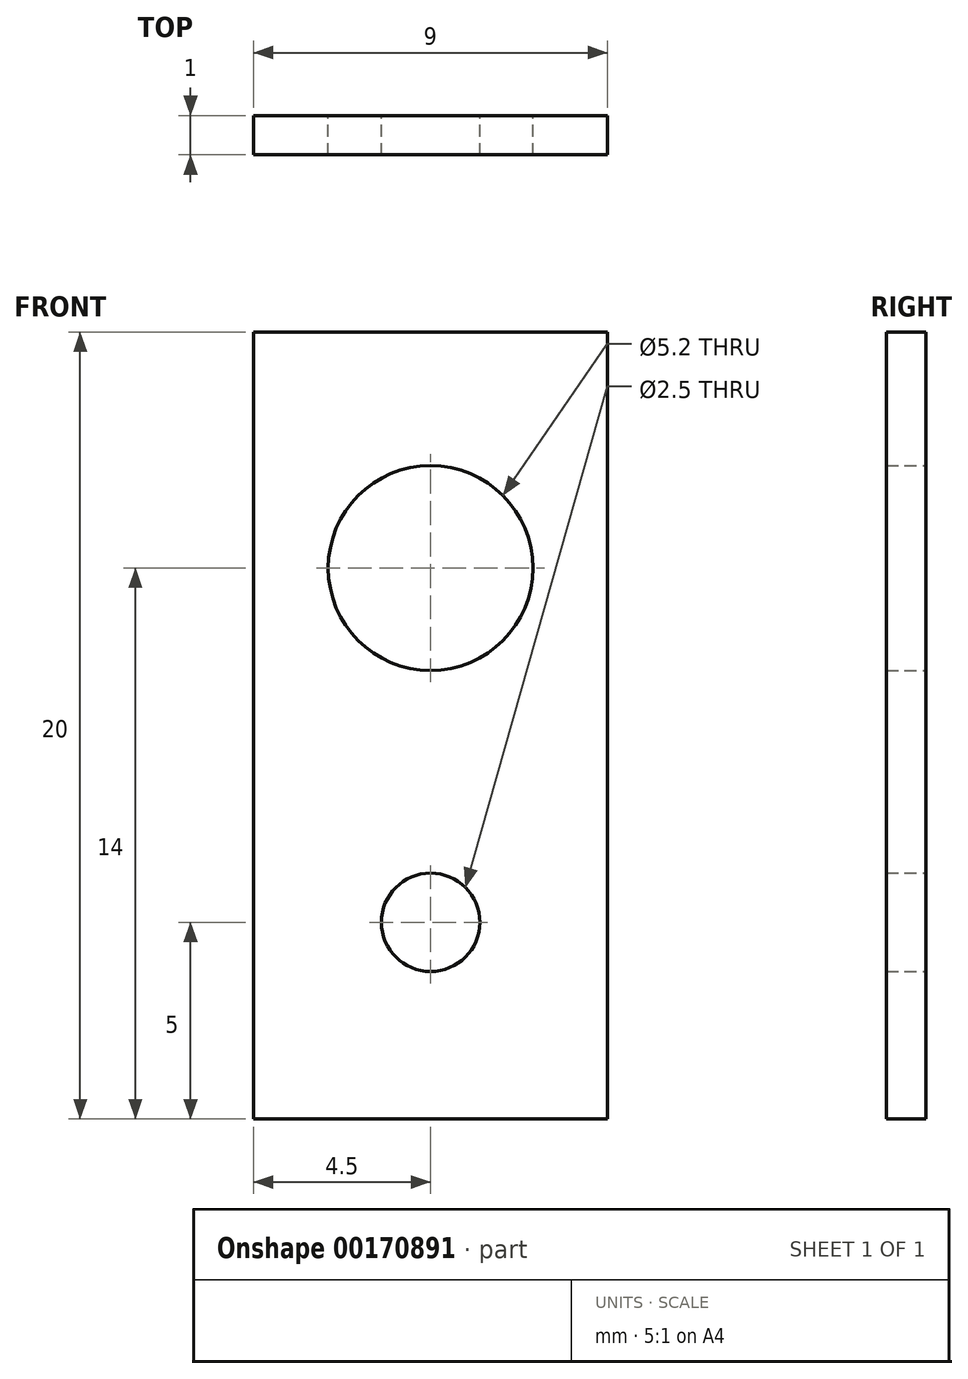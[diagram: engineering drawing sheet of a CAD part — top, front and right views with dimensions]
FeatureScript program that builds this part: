
annotation { "Feature Type Name" : "Feature", "Feature Type Description" : "" }
export const myFeature = defineFeature(function(context is Context, id is Id, definition is map)
    precondition{}
    {
        {
            var Q0;
            Q0=qCreatedBy(makeId("Front.planeOp"),FACE);
            var sketch = newSketch(context, id + "F0", { "sketchPlane" : qUnion([Q0])});
            skLineSegment(sketch, "E0.bottom", {"start": v(-4.5, 10) * mm, "end": v(4.5, 10) * mm});
            skLineSegment(sketch, "E0.top", {"start": v(-4.5, -10) * mm, "end": v(4.5, -10) * mm});
            skLineSegment(sketch, "E0.left", {"start": v(-4.5, 10) * mm, "end": v(-4.5, -10) * mm});
            skLineSegment(sketch, "E0.right", {"start": v(4.5, 10) * mm, "end": v(4.5, -10) * mm});
            skPoint(sketch, "E0.middle", {"position": v(0, 0) * mm});
            skCircle(sketch, "E1", {"center": v(0, 4) * mm, "radius": 2.6 * mm});
            skCircle(sketch, "E2", {"center": v(0, -5) * mm, "radius": 1.25 * mm});
            skSolve(sketch);
        }
        {
            var Q0;
            Q0=makeQuery(id+"F0.imprint","IMPRINT",FACE,{"disambiguationData":[TD([[makeQuery(id+"F0.imprint","IMPRINT",EDGE,{"derivedFrom":sQuery(id+"F0.wireOp",EDGE,"E0.bottom")}),-1.0]])]});
            extrude(context, id + "F1", {"entities" : qUnion([Q0]), "depth" : 1 * mm});
        }
    });
